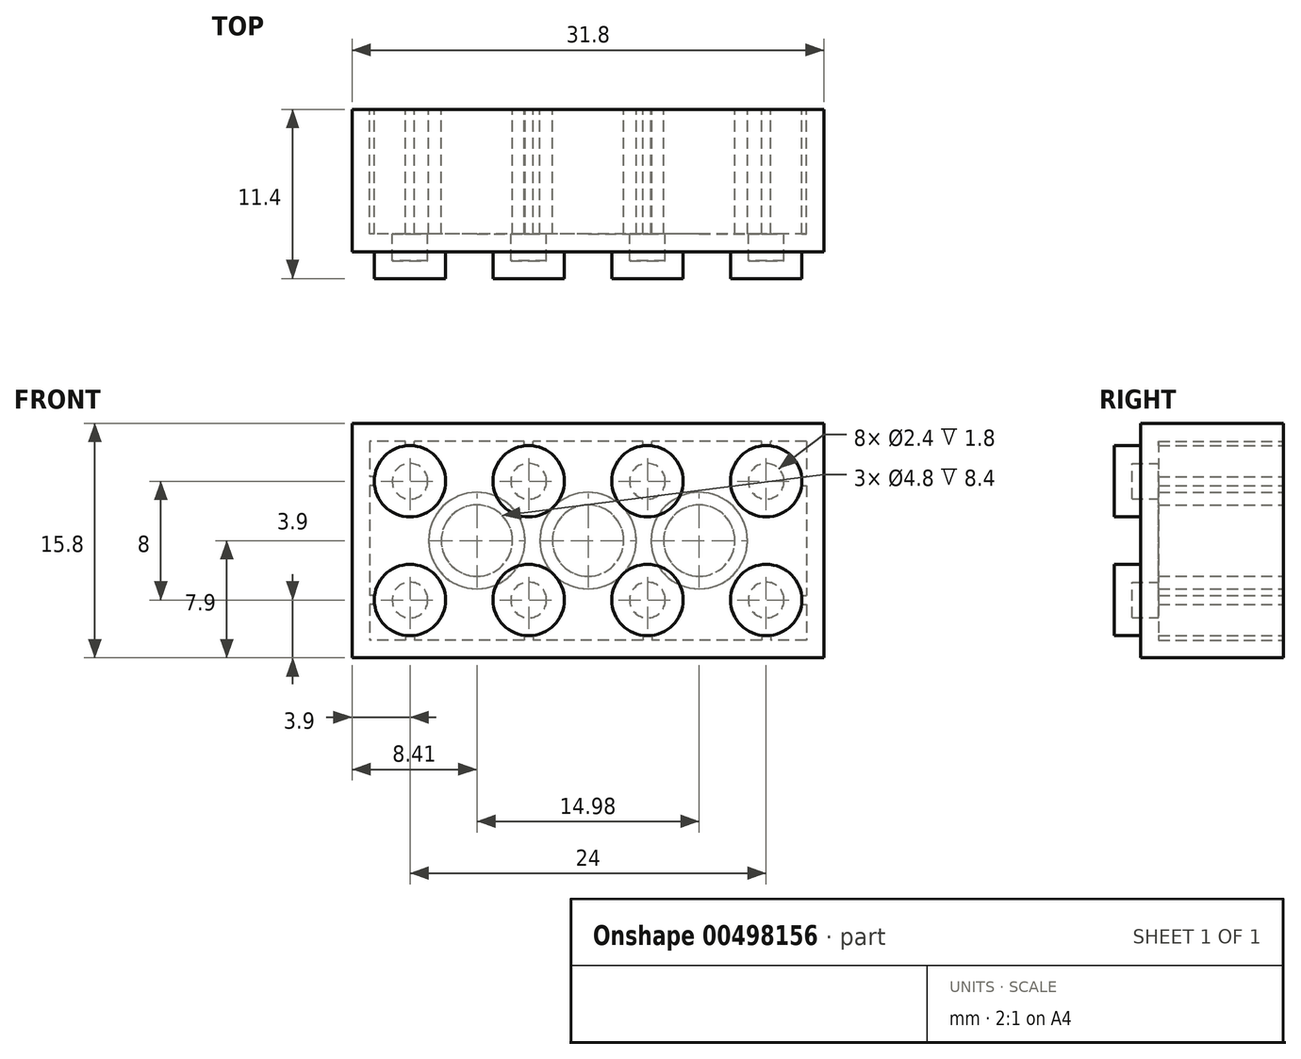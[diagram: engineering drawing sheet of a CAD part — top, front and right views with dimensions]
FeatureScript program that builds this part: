
annotation { "Feature Type Name" : "Feature", "Feature Type Description" : "" }
export const myFeature = defineFeature(function(context is Context, id is Id, definition is map)
    precondition{}
    {
        {
            var Q0;
            Q0=qCreatedBy(makeId("Front.planeOp"),FACE);
            var sketch = newSketch(context, id + "F0", { "sketchPlane" : qUnion([Q0])});
            skLineSegment(sketch, "E0.bottom", {"start": v(15.9, 7.9) * mm, "end": v(-15.9, 7.9) * mm});
            skLineSegment(sketch, "E0.top", {"start": v(15.9, -7.9) * mm, "end": v(-15.9, -7.9) * mm});
            skLineSegment(sketch, "E0.left", {"start": v(15.9, 7.9) * mm, "end": v(15.9, -7.9) * mm});
            skLineSegment(sketch, "E0.right", {"start": v(-15.9, 7.9) * mm, "end": v(-15.9, -7.9) * mm});
            skPoint(sketch, "E0.middle", {"position": v(0, 0) * mm});
            skSolve(sketch);
        }
        {
            var Q0;
            Q0=makeQuery(id+"F0.imprint","IMPRINT",FACE,{"disambiguationData":[TD([[makeQuery(id+"F0.imprint","IMPRINT",EDGE,{"derivedFrom":sQuery(id+"F0.wireOp",EDGE,"E0.bottom")}),1.0]])]});
            extrude(context, id + "F1", {"entities" : qUnion([Q0]), "depth" : 9.6 * mm});
        }
        {
            var Q0;
            Q0=makeQuery(id+"F1.opExtrude","CAP_FACE",FACE,{"disambiguationData":[OSD([sQuery(id+"F0.wireOp",EDGE,"E0.bottom"),sQuery(id+"F0.wireOp",EDGE,"E0.top"),sQuery(id+"F0.wireOp",EDGE,"E0.left"),sQuery(id+"F0.wireOp",EDGE,"E0.right")])],"isStart":false});
            var sketch = newSketch(context, id + "F2", { "sketchPlane" : qUnion([Q0])});
            skCircle(sketch, "E1", {"center": v(-12, 4) * mm, "radius": 2.4 * mm});
            skCircle(sketch, "E2.1.0.0", {"center": v(-4, 4) * mm, "radius": 2.4 * mm});
            skCircle(sketch, "E2.2.0.0", {"center": v(4, 4) * mm, "radius": 2.4 * mm});
            skCircle(sketch, "E2.3.0.0", {"center": v(12, 4) * mm, "radius": 2.4 * mm});
            skLineSegment(sketch, "E2.direction1", {"start": v(-12, 4) * mm, "end": v(-4, 4) * mm, "construction": true});
            skCircle(sketch, "E3", {"center": v(-12, -4) * mm, "radius": 2.4 * mm});
            skCircle(sketch, "E4.1.0.0", {"center": v(-4, -4) * mm, "radius": 2.4 * mm});
            skCircle(sketch, "E4.2.0.0", {"center": v(4, -4) * mm, "radius": 2.4 * mm});
            skCircle(sketch, "E4.3.0.0", {"center": v(12, -4) * mm, "radius": 2.4 * mm});
            skLineSegment(sketch, "E4.direction1", {"start": v(-12, -4) * mm, "end": v(-4, -4) * mm, "construction": true});
            skSolve(sketch);
        }
        {
            var Q0;
            Q0=makeQuery(id+"F2.imprint","IMPRINT",FACE,{"disambiguationData":[TD([[makeQuery(id+"F2.imprint","IMPRINT",EDGE,{"derivedFrom":sQuery(id+"F2.wireOp",EDGE,"E1")}),1.0]])]});
            var Q1;
            Q1=makeQuery(id+"F2.imprint","IMPRINT",FACE,{"disambiguationData":[TD([[makeQuery(id+"F2.imprint","IMPRINT",EDGE,{"derivedFrom":sQuery(id+"F2.wireOp",EDGE,"E2.1.0.0")}),1.0]])]});
            var Q2;
            Q2=makeQuery(id+"F2.imprint","IMPRINT",FACE,{"disambiguationData":[TD([[makeQuery(id+"F2.imprint","IMPRINT",EDGE,{"derivedFrom":sQuery(id+"F2.wireOp",EDGE,"E2.2.0.0")}),1.0]])]});
            var Q3;
            Q3=makeQuery(id+"F2.imprint","IMPRINT",FACE,{"disambiguationData":[TD([[makeQuery(id+"F2.imprint","IMPRINT",EDGE,{"derivedFrom":sQuery(id+"F2.wireOp",EDGE,"E2.3.0.0")}),1.0]])]});
            var Q4;
            Q4=makeQuery(id+"F2.imprint","IMPRINT",FACE,{"disambiguationData":[TD([[makeQuery(id+"F2.imprint","IMPRINT",EDGE,{"derivedFrom":sQuery(id+"F2.wireOp",EDGE,"E3")}),1.0]])]});
            var Q5;
            Q5=makeQuery(id+"F2.imprint","IMPRINT",FACE,{"disambiguationData":[TD([[makeQuery(id+"F2.imprint","IMPRINT",EDGE,{"derivedFrom":sQuery(id+"F2.wireOp",EDGE,"E4.1.0.0")}),1.0]])]});
            var Q6;
            Q6=makeQuery(id+"F2.imprint","IMPRINT",FACE,{"disambiguationData":[TD([[makeQuery(id+"F2.imprint","IMPRINT",EDGE,{"derivedFrom":sQuery(id+"F2.wireOp",EDGE,"E4.2.0.0")}),1.0]])]});
            var Q7;
            Q7=makeQuery(id+"F2.imprint","IMPRINT",FACE,{"disambiguationData":[TD([[makeQuery(id+"F2.imprint","IMPRINT",EDGE,{"derivedFrom":sQuery(id+"F2.wireOp",EDGE,"E4.3.0.0")}),1.0]])]});
            extrude(context, id + "F3", {"entities" : qUnion([Q0, Q1, Q2, Q3, Q4, Q5, Q6, Q7]), "operationType" : NewBodyOperationType.ADD, "depth" : 1.8 * mm});
        }
        {
            var Q0;
            Q0=makeQuery(id+"F1.opExtrude","CAP_FACE",FACE,{"disambiguationData":[OSD([sQuery(id+"F0.wireOp",EDGE,"E0.bottom"),sQuery(id+"F0.wireOp",EDGE,"E0.top"),sQuery(id+"F0.wireOp",EDGE,"E0.left"),sQuery(id+"F0.wireOp",EDGE,"E0.right")])],"isStart":true});
            var sketch = newSketch(context, id + "F4", { "sketchPlane" : qUnion([Q0])});
            skLineSegment(sketch, "E5.bottom", {"start": v(-14.7, -6.7) * mm, "end": v(14.7, -6.7) * mm});
            skLineSegment(sketch, "E5.top", {"start": v(-14.7, 6.7) * mm, "end": v(14.7, 6.7) * mm});
            skLineSegment(sketch, "E5.left", {"start": v(-14.7, -6.7) * mm, "end": v(-14.7, 6.7) * mm});
            skLineSegment(sketch, "E5.right", {"start": v(14.7, -6.7) * mm, "end": v(14.7, 6.7) * mm});
            skPoint(sketch, "E5.middle", {"position": v(0, 0) * mm});
            skCircle(sketch, "E6", {"center": v(0, 0) * mm, "radius": 2.4 * mm});
            skCircle(sketch, "E7", {"center": v(0, 0) * mm, "radius": 3.25 * mm});
            skLineSegment(sketch, "E8.direction1", {"start": v(0, 0) * mm, "end": v(7.5, 0) * mm, "construction": true});
            skCircle(sketch, "E9.0.1.0", {"center": v(7.5, 0) * mm, "radius": 2.4 * mm});
            skCircle(sketch, "E9.2.1.0", {"center": v(7.5, 0) * mm, "radius": 3.25 * mm});
            skCircle(sketch, "E10.1.0.0", {"center": v(-7.5, 0) * mm, "radius": 2.4 * mm});
            skCircle(sketch, "E10.1.0.1", {"center": v(-7.5, 0) * mm, "radius": 3.25 * mm});
            skLineSegment(sketch, "E10.direction1", {"start": v(0, 0) * mm, "end": v(-7.5, 0) * mm, "construction": true});
            skPoint(sketch, "E11.endSnap0", {"position": v(15.9, 0) * mm});
            skPoint(sketch, "E12.middle", {"position": v(12.07, -6.55) * mm});
            skSolve(sketch);
        }
        {
            var Q0;
            Q0=makeQuery(id+"F1.opExtrude","CAP_FACE",FACE,{"disambiguationData":[OSD([sQuery(id+"F0.wireOp",EDGE,"E0.bottom"),sQuery(id+"F0.wireOp",EDGE,"E0.top"),sQuery(id+"F0.wireOp",EDGE,"E0.left"),sQuery(id+"F0.wireOp",EDGE,"E0.right")])],"isStart":true});
            shell(context, id + "F5", {"entities" : qUnion([Q0]), "thickness" : 1.2 * mm});
        }
        {
            var Q0;
            Q0=makeQuery(id+"F4.imprint","IMPRINT",FACE,{"disambiguationData":[TD([[makeQuery(id+"F4.imprint","IMPRINT",EDGE,{"derivedFrom":sQuery(id+"F4.wireOp",EDGE,"E9.0.1.0")}),-1.0]])]});
            var Q1;
            Q1=makeQuery(id+"F4.imprint","IMPRINT",FACE,{"disambiguationData":[TD([[makeQuery(id+"F4.imprint","IMPRINT",EDGE,{"derivedFrom":sQuery(id+"F4.wireOp",EDGE,"E6")}),-1.0]])]});
            var Q2;
            Q2=makeQuery(id+"F4.imprint","IMPRINT",FACE,{"disambiguationData":[TD([[makeQuery(id+"F4.imprint","IMPRINT",EDGE,{"derivedFrom":sQuery(id+"F4.wireOp",EDGE,"E10.1.0.0")}),-1.0]])]});
            extrude(context, id + "F6", {"entities" : qUnion([Q0, Q1, Q2]), "operationType" : NewBodyOperationType.ADD, "oppositeDirection" : true, "depth" : 9.6 * mm});
        }
        {
            var Q0;
            Q0=makeQuery(id+"F1.opExtrude","CAP_FACE",FACE,{"disambiguationData":[OSD([sQuery(id+"F0.wireOp",EDGE,"E0.bottom"),sQuery(id+"F0.wireOp",EDGE,"E0.top"),sQuery(id+"F0.wireOp",EDGE,"E0.left"),sQuery(id+"F0.wireOp",EDGE,"E0.right")])],"isStart":true});
            var sketch = newSketch(context, id + "F7", { "sketchPlane" : qUnion([Q0])});
            skLineSegment(sketch, "E13", {"start": v(15.9, -7.9) * mm, "end": v(15.9, -4) * mm, "construction": true});
            skLineSegment(sketch, "E14", {"start": v(15.9, -4) * mm, "end": v(12, -4) * mm, "construction": true});
            skLineSegment(sketch, "E15", {"start": v(12, -4) * mm, "end": v(12, -7.9) * mm, "construction": true});
            skLineSegment(sketch, "E16.bottom", {"start": v(11.7, -6.7) * mm, "end": v(12.3, -6.7) * mm});
            skLineSegment(sketch, "E16.top", {"start": v(11.7, -6.4) * mm, "end": v(12.3, -6.4) * mm});
            skLineSegment(sketch, "E16.left", {"start": v(11.7, -6.7) * mm, "end": v(11.7, -6.4) * mm});
            skLineSegment(sketch, "E16.right", {"start": v(12.3, -6.7) * mm, "end": v(12.3, -6.4) * mm});
            skPoint(sketch, "E16.middle", {"position": v(12, -6.55) * mm});
            skLineSegment(sketch, "E17.1.0.0", {"start": v(4.3, -6.7) * mm, "end": v(4.3, -6.4) * mm});
            skLineSegment(sketch, "E17.1.0.1", {"start": v(3.7, -6.4) * mm, "end": v(4.3, -6.4) * mm});
            skLineSegment(sketch, "E17.1.0.2", {"start": v(3.7, -6.7) * mm, "end": v(3.7, -6.4) * mm});
            skLineSegment(sketch, "E17.2.0.0", {"start": v(-3.7, -6.7) * mm, "end": v(-3.7, -6.4) * mm});
            skLineSegment(sketch, "E17.2.0.1", {"start": v(-4.3, -6.4) * mm, "end": v(-3.7, -6.4) * mm});
            skLineSegment(sketch, "E17.2.0.2", {"start": v(-4.3, -6.7) * mm, "end": v(-4.3, -6.4) * mm});
            skLineSegment(sketch, "E17.3.0.0", {"start": v(-11.7, -6.7) * mm, "end": v(-11.7, -6.4) * mm});
            skLineSegment(sketch, "E17.3.0.1", {"start": v(-12.3, -6.4) * mm, "end": v(-11.7, -6.4) * mm});
            skLineSegment(sketch, "E17.3.0.2", {"start": v(-12.3, -6.7) * mm, "end": v(-12.3, -6.4) * mm});
            skLineSegment(sketch, "E17.direction1", {"start": v(12.3, -6.7) * mm, "end": v(4.3, -6.7) * mm, "construction": true});
            skLineSegment(sketch, "E18", {"start": v(15.9, 7.9) * mm, "end": v(15.9, 4) * mm, "construction": true});
            skLineSegment(sketch, "E19", {"start": v(15.9, 4) * mm, "end": v(12, 4) * mm, "construction": true});
            skLineSegment(sketch, "E20", {"start": v(12, 4) * mm, "end": v(12, 7.9) * mm, "construction": true});
            skLineSegment(sketch, "E21.bottom", {"start": v(11.7, 6.7) * mm, "end": v(12.3, 6.7) * mm});
            skLineSegment(sketch, "E21.top", {"start": v(11.7, 6.4) * mm, "end": v(12.3, 6.4) * mm});
            skLineSegment(sketch, "E21.left", {"start": v(11.7, 6.7) * mm, "end": v(11.7, 6.4) * mm});
            skLineSegment(sketch, "E21.right", {"start": v(12.3, 6.7) * mm, "end": v(12.3, 6.4) * mm});
            skPoint(sketch, "E21.middle", {"position": v(12, 6.55) * mm});
            skLineSegment(sketch, "E22.1.0.0", {"start": v(4.3, 6.7) * mm, "end": v(4.3, 6.4) * mm});
            skLineSegment(sketch, "E22.1.0.1", {"start": v(3.7, 6.4) * mm, "end": v(4.3, 6.4) * mm});
            skLineSegment(sketch, "E22.1.0.2", {"start": v(3.7, 6.7) * mm, "end": v(3.7, 6.4) * mm});
            skLineSegment(sketch, "E22.2.0.0", {"start": v(-3.7, 6.7) * mm, "end": v(-3.7, 6.4) * mm});
            skLineSegment(sketch, "E22.2.0.1", {"start": v(-4.3, 6.4) * mm, "end": v(-3.7, 6.4) * mm});
            skLineSegment(sketch, "E22.2.0.2", {"start": v(-4.3, 6.7) * mm, "end": v(-4.3, 6.4) * mm});
            skLineSegment(sketch, "E22.3.0.0", {"start": v(-11.7, 6.7) * mm, "end": v(-11.7, 6.4) * mm});
            skLineSegment(sketch, "E22.3.0.1", {"start": v(-12.3, 6.4) * mm, "end": v(-11.7, 6.4) * mm});
            skLineSegment(sketch, "E22.3.0.2", {"start": v(-12.3, 6.7) * mm, "end": v(-12.3, 6.4) * mm});
            skLineSegment(sketch, "E22.direction1", {"start": v(12.3, 6.4) * mm, "end": v(4.3, 6.4) * mm, "construction": true});
            skLineSegment(sketch, "E23.bottom", {"start": v(14.7, -3.7) * mm, "end": v(14.4, -3.7) * mm});
            skLineSegment(sketch, "E23.top", {"start": v(14.7, -4.3) * mm, "end": v(14.4, -4.3) * mm});
            skLineSegment(sketch, "E23.left", {"start": v(14.7, -3.7) * mm, "end": v(14.7, -4.3) * mm});
            skLineSegment(sketch, "E23.right", {"start": v(14.4, -3.7) * mm, "end": v(14.4, -4.3) * mm});
            skPoint(sketch, "E23.middle", {"position": v(14.55, -4) * mm});
            skLineSegment(sketch, "E24.bottom", {"start": v(14.7, 4.3) * mm, "end": v(14.4, 4.3) * mm});
            skLineSegment(sketch, "E24.top", {"start": v(14.7, 3.7) * mm, "end": v(14.4, 3.7) * mm});
            skLineSegment(sketch, "E24.left", {"start": v(14.7, 4.3) * mm, "end": v(14.7, 3.7) * mm});
            skLineSegment(sketch, "E24.right", {"start": v(14.4, 4.3) * mm, "end": v(14.4, 3.7) * mm});
            skPoint(sketch, "E24.middle", {"position": v(14.55, 4) * mm});
            skLineSegment(sketch, "E25", {"start": v(0, -6.7) * mm, "end": v(0, -4.05) * mm, "construction": true});
            skPoint(sketch, "E25.endSnap0", {"position": v(0, -6.7) * mm});
            skLineSegment(sketch, "E26", {"start": v(-15.9, -7.9) * mm, "end": v(-15.9, -4) * mm, "construction": true});
            skLineSegment(sketch, "E27", {"start": v(-15.9, -4) * mm, "end": v(-12, -4) * mm, "construction": true});
            skLineSegment(sketch, "E28", {"start": v(-12, -4) * mm, "end": v(-12, -7.9) * mm, "construction": true});
            skLineSegment(sketch, "E29", {"start": v(-15.9, 7.9) * mm, "end": v(-15.9, 4) * mm, "construction": true});
            skLineSegment(sketch, "E30", {"start": v(-15.9, 4) * mm, "end": v(-12, 4) * mm, "construction": true});
            skLineSegment(sketch, "E31", {"start": v(-12, 4) * mm, "end": v(-12, 7.9) * mm, "construction": true});
            skLineSegment(sketch, "E32.bottom", {"start": v(-14.7, -4.3) * mm, "end": v(-14.4, -4.3) * mm});
            skLineSegment(sketch, "E32.top", {"start": v(-14.7, -3.7) * mm, "end": v(-14.4, -3.7) * mm});
            skLineSegment(sketch, "E32.left", {"start": v(-14.7, -4.3) * mm, "end": v(-14.7, -3.7) * mm});
            skLineSegment(sketch, "E32.right", {"start": v(-14.4, -4.3) * mm, "end": v(-14.4, -3.7) * mm});
            skPoint(sketch, "E32.middle", {"position": v(-14.55, -4) * mm});
            skLineSegment(sketch, "E33.bottom", {"start": v(-14.7, 3.7) * mm, "end": v(-14.4, 3.7) * mm});
            skLineSegment(sketch, "E33.top", {"start": v(-14.7, 4.3) * mm, "end": v(-14.4, 4.3) * mm});
            skLineSegment(sketch, "E33.left", {"start": v(-14.7, 3.7) * mm, "end": v(-14.7, 4.3) * mm});
            skLineSegment(sketch, "E33.right", {"start": v(-14.4, 3.7) * mm, "end": v(-14.4, 4.3) * mm});
            skPoint(sketch, "E33.middle", {"position": v(-14.55, 4) * mm});
            skSolve(sketch);
        }
        {
            var Q0;
            {var subQ0=sQuery(id+"F7.wireOp",EDGE,"E17.1.0.0");Q0=makeQuery(id+"F7.imprint","IMPRINT",FACE,{"disambiguationData":[TD([[makeQuery(id+"F7.imprint","IMPRINT",EDGE,{"derivedFrom":subQ0}),1.0]])]});}
            var Q1;
            {var subQ0=sQuery(id+"F7.wireOp",EDGE,"E17.2.0.0");Q1=makeQuery(id+"F7.imprint","IMPRINT",FACE,{"disambiguationData":[TD([[makeQuery(id+"F7.imprint","IMPRINT",EDGE,{"derivedFrom":subQ0}),1.0]])]});}
            var Q2;
            {var subQ0=sQuery(id+"F7.wireOp",EDGE,"E17.3.0.0");Q2=makeQuery(id+"F7.imprint","IMPRINT",FACE,{"disambiguationData":[TD([[makeQuery(id+"F7.imprint","IMPRINT",EDGE,{"derivedFrom":subQ0}),1.0]])]});}
            var Q3;
            Q3=makeQuery(id+"F7.imprint","IMPRINT",FACE,{"disambiguationData":[TD([[makeQuery(id+"F7.imprint","IMPRINT",EDGE,{"derivedFrom":sQuery(id+"F7.wireOp",EDGE,"E32.bottom")}),1.0]])]});
            var Q4;
            Q4=makeQuery(id+"F7.imprint","IMPRINT",FACE,{"disambiguationData":[TD([[makeQuery(id+"F7.imprint","IMPRINT",EDGE,{"derivedFrom":sQuery(id+"F7.wireOp",EDGE,"E33.bottom")}),1.0]])]});
            var Q5;
            {var subQ0=sQuery(id+"F7.wireOp",EDGE,"E22.3.0.0");Q5=makeQuery(id+"F7.imprint","IMPRINT",FACE,{"disambiguationData":[TD([[makeQuery(id+"F7.imprint","IMPRINT",EDGE,{"derivedFrom":subQ0}),-1.0]])]});}
            var Q6;
            {var subQ0=sQuery(id+"F7.wireOp",EDGE,"E22.2.0.0");Q6=makeQuery(id+"F7.imprint","IMPRINT",FACE,{"disambiguationData":[TD([[makeQuery(id+"F7.imprint","IMPRINT",EDGE,{"derivedFrom":subQ0}),-1.0]])]});}
            var Q7;
            {var subQ0=sQuery(id+"F7.wireOp",EDGE,"E22.1.0.0");Q7=makeQuery(id+"F7.imprint","IMPRINT",FACE,{"disambiguationData":[TD([[makeQuery(id+"F7.imprint","IMPRINT",EDGE,{"derivedFrom":subQ0}),-1.0]])]});}
            var Q8;
            Q8=makeQuery(id+"F7.imprint","IMPRINT",FACE,{"disambiguationData":[TD([[makeQuery(id+"F7.imprint","IMPRINT",EDGE,{"derivedFrom":sQuery(id+"F7.wireOp",EDGE,"E21.bottom")}),-1.0]])]});
            var Q9;
            Q9=makeQuery(id+"F7.imprint","IMPRINT",FACE,{"disambiguationData":[TD([[makeQuery(id+"F7.imprint","IMPRINT",EDGE,{"derivedFrom":sQuery(id+"F7.wireOp",EDGE,"E16.bottom")}),1.0]])]});
            var Q10;
            Q10=makeQuery(id+"F7.imprint","IMPRINT",FACE,{"disambiguationData":[TD([[makeQuery(id+"F7.imprint","IMPRINT",EDGE,{"derivedFrom":sQuery(id+"F7.wireOp",EDGE,"E23.bottom")}),1.0]])]});
            var Q11;
            Q11=makeQuery(id+"F7.imprint","IMPRINT",FACE,{"disambiguationData":[TD([[makeQuery(id+"F7.imprint","IMPRINT",EDGE,{"derivedFrom":sQuery(id+"F7.wireOp",EDGE,"E24.bottom")}),1.0]])]});
            extrude(context, id + "F8", {"entities" : qUnion([Q0, Q1, Q2, Q3, Q4, Q5, Q6, Q7, Q8, Q9, Q10, Q11]), "operationType" : NewBodyOperationType.ADD, "oppositeDirection" : true, "depth" : 9.6 * mm});
        }
    });
